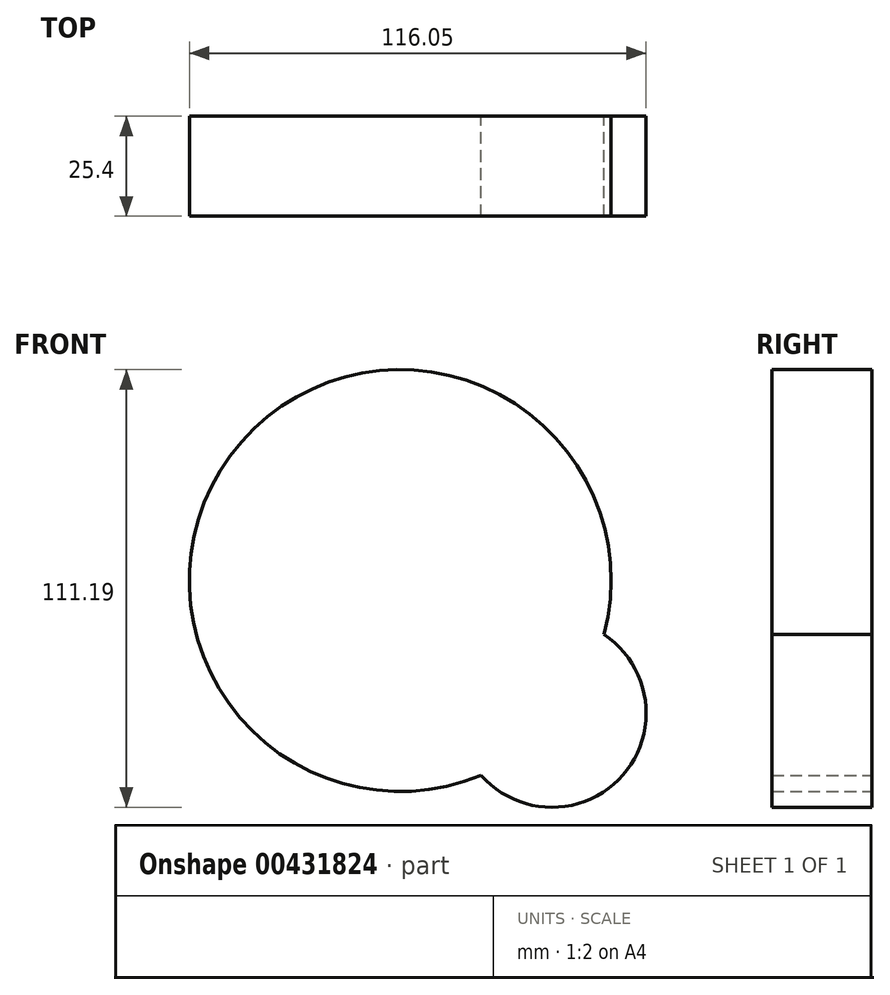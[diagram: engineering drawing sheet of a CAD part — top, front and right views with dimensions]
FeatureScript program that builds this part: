
annotation { "Feature Type Name" : "Feature", "Feature Type Description" : "" }
export const myFeature = defineFeature(function(context is Context, id is Id, definition is map)
    precondition{}
    {
        {
            var Q0;
            Q0=qCreatedBy(makeId("Front.planeOp"),FACE);
            var sketch = newSketch(context, id + "F0", { "sketchPlane" : qUnion([Q0])});
            skArc(sketch, "E0", {"start": v(-17.98, -49.48) * mm, "mid": v(18.03, -49.42) * mm, "end": v(13.27, -13.73) * mm});
            skArc(sketch, "E1", {"start": v(13.27, -13.73) * mm, "mid": v(-78.87, 35.26) * mm, "end": v(-17.98, -49.48) * mm});
            skSolve(sketch);
        }
        {
            var Q0;
            Q0=makeQuery(id+"F0.imprint","IMPRINT",FACE,{"disambiguationData":[TD([[makeQuery(id+"F0.imprint","IMPRINT",EDGE,{"derivedFrom":sQuery(id+"F0.wireOp",EDGE,"E0")}),1.0]])]});
            extrude(context, id + "F1", {"entities" : qUnion([Q0]), "depth" : 25.4 * mm});
        }
    });
